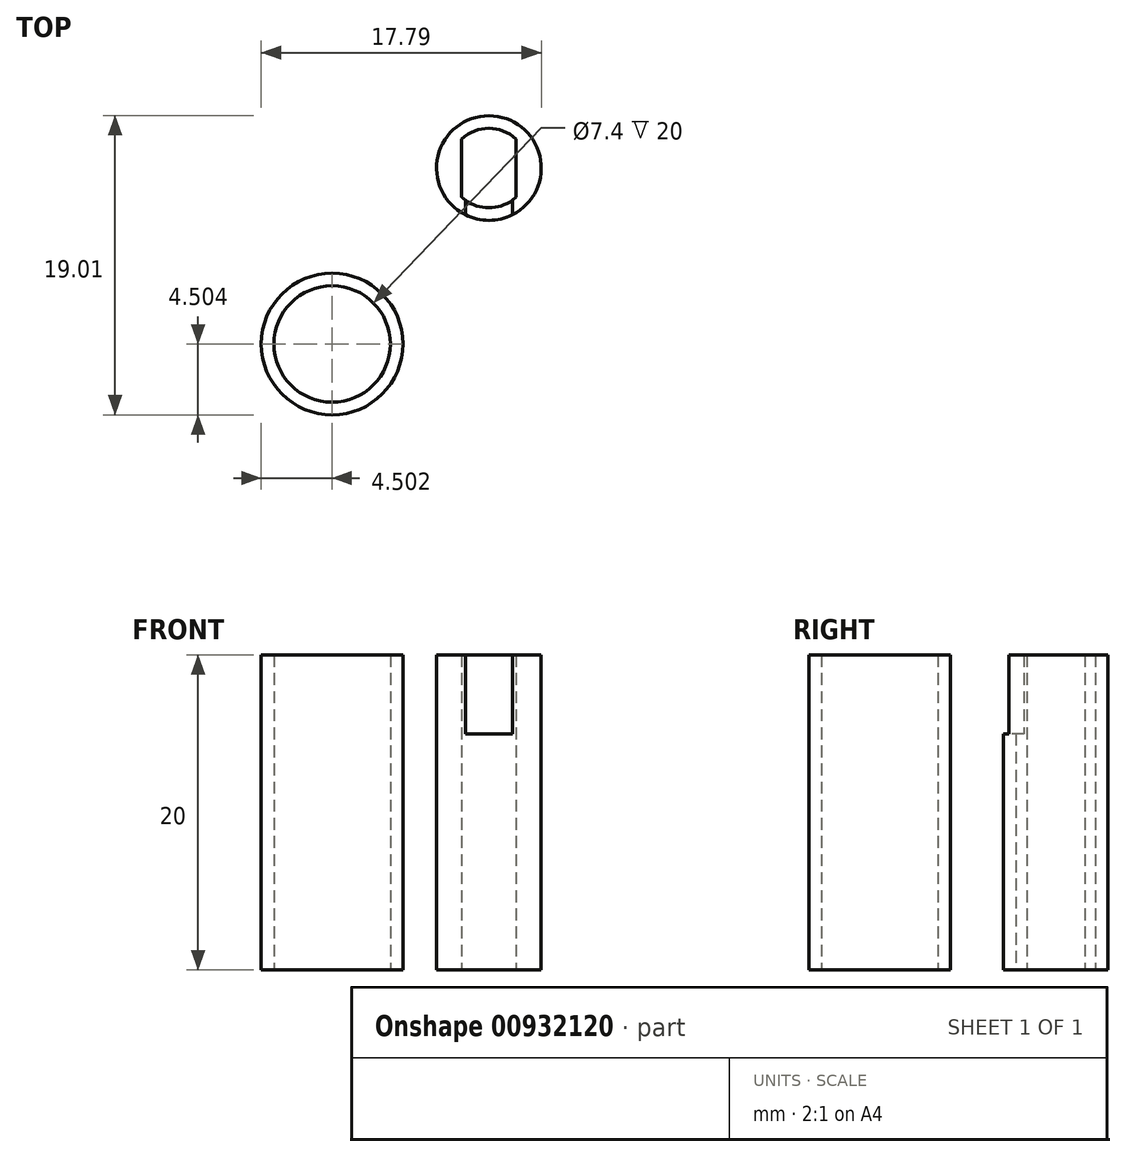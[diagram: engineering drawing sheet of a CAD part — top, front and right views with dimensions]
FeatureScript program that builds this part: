
annotation { "Feature Type Name" : "Feature", "Feature Type Description" : "" }
export const myFeature = defineFeature(function(context is Context, id is Id, definition is map)
    precondition{}
    {
        {
            var Q0;
            Q0=qCreatedBy(makeId("Top.planeOp"),FACE);
            var sketch = newSketch(context, id + "F0", { "sketchPlane" : qUnion([Q0])});
            skCircle(sketch, "E0", {"center": v(0, 0) * mm, "radius": 3.33 * mm});
            skCircle(sketch, "E1.0", {"center": v(0, 0) * mm, "radius": 2.53 * mm});
            skCircle(sketch, "E2", {"center": v(-9.96, -11.18) * mm, "radius": 3.7 * mm});
            skCircle(sketch, "E3.0", {"center": v(-9.96, -11.18) * mm, "radius": 4.5 * mm});
            skLineSegment(sketch, "E4", {"start": v(2.53, 0) * mm, "end": v(1.73, 0) * mm, "construction": true});
            skLineSegment(sketch, "E5", {"start": v(1.73, 0) * mm, "end": v(1.73, 1.84) * mm});
            skLineSegment(sketch, "E6.MirrorCS", {"start": v(1.73, 0) * mm, "end": v(1.73, -1.84) * mm});
            skLineSegment(sketch, "E7.MirrorCS", {"start": v(-1.73, 0) * mm, "end": v(-1.73, 1.84) * mm});
            skLineSegment(sketch, "E8.MirrorCS", {"start": v(-1.73, 0) * mm, "end": v(-1.73, -1.84) * mm});
            skSolve(sketch);
        }
        {
            var Q0;
            Q0=makeQuery(id+"F0.imprint","IMPRINT",FACE,{"disambiguationData":[TD([[makeQuery(id+"F0.imprint","IMPRINT",EDGE,{"derivedFrom":sQuery(id+"F0.wireOp",EDGE,"E0")}),1.0]])]});
            var Q1;
            {var subQ0=sQuery(id+"F0.wireOp",EDGE,"E7.MirrorCS");Q1=makeQuery(id+"F0.imprint","IMPRINT",FACE,{"disambiguationData":[TD([[makeQuery(id+"F0.imprint","IMPRINT",EDGE,{"derivedFrom":subQ0}),1.0]])]});}
            var Q2;
            {var subQ0=sQuery(id+"F0.wireOp",EDGE,"E5");Q2=makeQuery(id+"F0.imprint","IMPRINT",FACE,{"disambiguationData":[TD([[makeQuery(id+"F0.imprint","IMPRINT",EDGE,{"derivedFrom":subQ0}),-1.0]])]});}
            extrude(context, id + "F1", {"entities" : qUnion([Q0, Q1, Q2]), "depth" : 20 * mm, "offsetDistance" : 25 * mm});
        }
        {
            var Q0;
            Q0=makeQuery(id+"F0.imprint","IMPRINT",FACE,{"disambiguationData":[TD([[makeQuery(id+"F0.imprint","IMPRINT",EDGE,{"derivedFrom":sQuery(id+"F0.wireOp",EDGE,"E2")}),-1.0]])]});
            extrude(context, id + "F2", {"entities" : qUnion([Q0]), "depth" : 20 * mm, "offsetDistance" : 25 * mm});
        }
        {
            var Q0;
            Q0=makeQuery(id+"F1.opExtrude","CAP_FACE",FACE,{"disambiguationData":[OSD([sQuery(id+"F0.wireOp",EDGE,"E0"),sQuery(id+"F0.wireOp",EDGE,"E1.0")])],"isStart":false});
            var sketch = newSketch(context, id + "F3", { "sketchPlane" : qUnion([Q0])});
            skCircle(sketch, "E9.0", {"center": v(0, 0) * mm, "radius": 3.33 * mm});
            skCircle(sketch, "E10.0", {"center": v(0, 0) * mm, "radius": 2.53 * mm});
            skLineSegment(sketch, "E11", {"start": v(1.5, 2.03) * mm, "end": v(1.5, -2.97) * mm});
            skLineSegment(sketch, "E12.MirrorCS", {"start": v(-1.5, 2.03) * mm, "end": v(-1.5, -2.97) * mm});
            skSolve(sketch);
        }
        {
            var Q0;
            {var subQ0=sQuery(id+"F3.wireOp",EDGE,"E11");Q0=makeQuery(id+"F3.imprint","IMPRINT",FACE,{"disambiguationData":[TD([[makeQuery(id+"F3.imprint","IMPRINT",EDGE,{"derivedFrom":subQ0}),-1.0]])]});}
            extrude(context, id + "F4", {"entities" : qUnion([Q0]), "operationType" : NewBodyOperationType.REMOVE, "oppositeDirection" : true, "depth" : 5 * mm, "offsetDistance" : 25 * mm});
        }
    });
